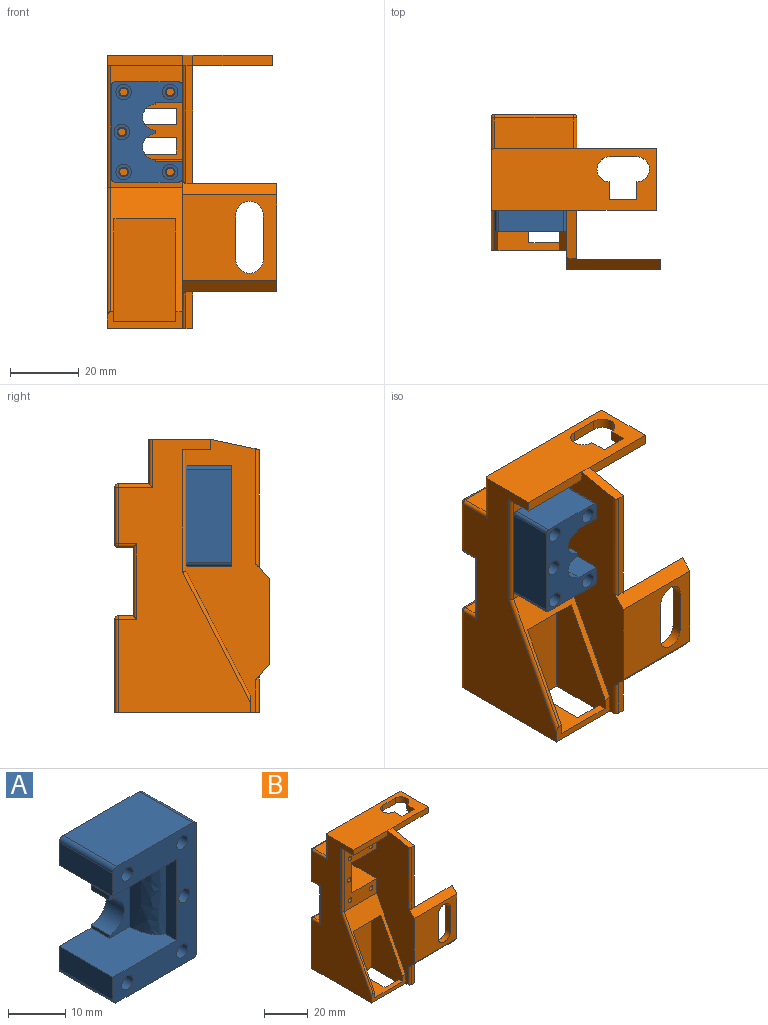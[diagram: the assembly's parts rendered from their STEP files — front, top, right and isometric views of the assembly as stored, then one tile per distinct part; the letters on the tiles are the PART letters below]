
ASSEMBLY  parts=2 mates=1
PART A: 36 faces, bbox 20.8x13.3x29.2 mm
  f0: extruded ~17.4x6mm, area 122.2mm2, adj f3,f5,f6,f14
  f1: plane 13.3x4.9mm, normal (-1,0,0), area 65.2mm2, adj f2,f3,f13,f34
  f2: plane 29.2x20.8mm, normal (0,-1,0), area 300.8mm2, adj f1,f3,f4,f5,f12,f14,f15,f16
  f3: plane 15.8x13.3mm, normal (0,0,-1), area 161.7mm2, adj f0,f1,f2,f6,f11,f13,f14
  f4: plane 13.3x4.9mm, normal (-1,0,0), area 65.2mm2, adj f2,f5,f13,f32
  f5: plane 15.8x13.3mm, normal (0,0,1), area 161.7mm2, adj f0,f2,f4,f6,f7,f13,f14
  f6: plane 17.4x5mm, normal (0,-1,0), area 42.8mm2, adj f0,f3,f5,f7,f8,f9,f10,f11
  f7: plane 4.5x0.65mm, normal (-1,0,0), area 2.9mm2, adj f5,f6,f8,f13
  f8: cylinder r=3.75mm len=7.5mm, axis (0,-1,0), area 53mm2, adj f6,f7,f9,f13
  f9: plane 4.5x1.1mm, normal (-1,0,0), area 5mm2, adj f6,f8,f10,f13
  f10: cylinder r=3.75mm len=7.5mm, axis (0,-1,0), area 53mm2, adj f6,f9,f11,f13
  f11: plane 4.5x0.65mm, normal (-1,0,0), area 2.9mm2, adj f3,f6,f10,f13
  f12: plane 27.2x13.3mm, normal (1,0,0), area 361.8mm2, adj f2,f13,f33,f35
  f13: plane 29.2x20.8mm, normal (0,1,0), area 345.3mm2, adj f1,f3,f4,f5,f7,f8,f9,f10
  f14: plane 17.4x2.8mm, normal (-1,0,0), area 48.7mm2, adj f0,f2,f3,f5
  f15: plane 18.8x13.3mm, normal (0,0,-1), area 250mm2, adj f2,f13,f32,f33
  f16: plane 18.8x13.3mm, normal (0,0,1), area 250mm2, adj f2,f13,f34,f35
  f17: cylinder r=2.25mm len=9.8mm, axis (0,1,0), area 138.5mm2, adj f13,f18
  f18: plane 4.5x4.5mm, normal (0,1,0), area 9.7mm2, adj f17,f31
  f19: cylinder r=2.25mm len=9.8mm, axis (0,1,0), area 138.5mm2, adj f13,f20
  f20: plane 4.5x4.5mm, normal (0,1,0), area 9.7mm2, adj f19,f30
  f21: cylinder r=2.25mm len=9.8mm, axis (0,1,0), area 138.5mm2, adj f13,f22
  f22: plane 4.5x4.5mm, normal (0,1,0), area 9.7mm2, adj f21,f29
  f23: cylinder r=2.25mm len=9.8mm, axis (0,1,0), area 138.5mm2, adj f13,f24
  f24: plane 4.5x4.5mm, normal (0,1,0), area 9.7mm2, adj f23,f28
  f25: cylinder r=2.25mm len=9.8mm, axis (0,1,0), area 138.5mm2, adj f13,f26
  f26: plane 4.5x4.5mm, normal (0,1,0), area 9.7mm2, adj f25,f27
  f27: cylinder r=1.4mm len=3.5mm, axis (0,1,0), area 30.8mm2, adj f2,f26
  f28: cylinder r=1.4mm len=3.5mm, axis (0,1,0), area 30.8mm2, adj f2,f24
  f29: cylinder r=1.4mm len=3.5mm, axis (0,1,0), area 30.8mm2, adj f2,f22
  f30: cylinder r=1.4mm len=3.5mm, axis (0,1,0), area 30.8mm2, adj f2,f20
  f31: cylinder r=1.4mm len=3.5mm, axis (0,1,0), area 30.8mm2, adj f2,f18
  f32: cylinder r=1mm len=13.3mm, axis (0,1,0), area 20.9mm2, adj f2,f4,f13,f15
  f33: cylinder r=1mm len=13.3mm, axis (0,1,0), area 20.9mm2, adj f2,f12,f13,f15
  f34: cylinder r=1mm len=13.3mm, axis (0,-1,0), area 20.9mm2, adj f1,f2,f13,f16
  f35: cylinder r=1mm len=13.3mm, axis (0,-1,0), area 20.9mm2, adj f2,f12,f13,f16
PART B: 94 faces, bbox 49.5x45.1x79.7 mm
  f0: plane 23.15x3mm, normal (0,-1,0), area 69.5mm2, adj f7,f40,f47,f50
  f1: plane 27.2x23mm, normal (0,1,0), area 625.6mm2, adj f30,f66,f68,f69
  f2: plane 79.7x38.6mm, normal (-1,0,0), area 1695.4mm2, adj f6,f30,f46,f50,f51,f68,f73,f77
  f3: plane 23x16.5mm, normal (0,1,0), area 261.4mm2, adj f16,f17,f18,f19,f20,f21,f22,f23
  f4: plane 10.7x2mm, normal (0,-1,0), area 21.4mm2, adj f7,f30,f39,f88
  f5: plane 34.4x2mm, normal (0,-1,0), area 68.8mm2, adj f7,f38,f89,f93
  f6: plane 22x5mm, normal (0,-1,0), area 55.5mm2, adj f2,f8,f12,f13,f27,f28,f30,f91
  f7: plane 79.7x41.1mm, normal (1,0,0), area 2953.5mm2, adj f0,f4,f5,f30,f31,f40,f48,f66
  f8: plane 32x20mm, normal (-1,0,0), area 446mm2, adj f6,f9,f11,f12,f28,f29,f30
  f9: plane 32x18mm, normal (0,-1,0), area 558mm2, adj f8,f10,f27,f28,f29,f30
  f10: plane 17.65x2mm, normal (1,0,0), area 35.3mm2, adj f9,f11,f28,f30
  f11: plane 9x2mm, normal (0,1,0), area 18mm2, adj f8,f10,f28,f30
  f12: plane 36.2x21mm, normal (0,-0.89,0.46), area 309mm2, adj f6,f8,f13,f14,f27,f29,f91
  f13: plane 79.7x42.3mm, normal (-1,0,0), area 1563.9mm2, adj f6,f12,f14,f15,f24,f26,f30,f37
  f14: plane 35.5x21mm, normal (0,-1,0), area 455.9mm2, adj f12,f13,f24,f25,f26,f51,f53,f55
  f15: plane 16.8x16mm, normal (0,-1,0), area 150.7mm2, adj f13,f16,f17,f18,f19,f20,f21,f22
  f16: plane 4.8x2.8mm, normal (-1,0,0), area 13.4mm2, adj f3,f15,f17,f22
  f17: plane 12.3x2.8mm, normal (0,0,1), area 34.4mm2, adj f3,f15,f16,f18
  f18: plane 4.8x2.8mm, normal (1,0,0), area 13.4mm2, adj f3,f15,f17,f22
  f19: plane 4.8x2.8mm, normal (-1,0,0), area 13.4mm2, adj f3,f15,f20,f23
  f20: plane 12.3x2.8mm, normal (0,0,1), area 34.4mm2, adj f3,f15,f19,f21
  f21: plane 4.8x2.8mm, normal (1,0,0), area 13.4mm2, adj f3,f15,f20,f23
  f22: plane 12.3x2.8mm, normal (0,0,-1), area 34.4mm2, adj f3,f15,f16,f18
  f23: plane 12.3x2.8mm, normal (0,0,-1), area 34.4mm2, adj f3,f15,f19,f21
  f24: plane 18x16mm, normal (0,0,1), area 288mm2, adj f13,f14,f15,f25
  f25: plane 18x16.8mm, normal (1,0,0), area 302.4mm2, adj f14,f15,f24,f26
  f26: plane 18x16mm, normal (0,0,-1), area 288mm2, adj f13,f14,f15,f25
  f27: plane 30x20mm, normal (1,0,0), area 410.7mm2, adj f6,f9,f12,f28,f29
  f28: plane 20x18mm, normal (0,0,1), area 201.2mm2, adj f6,f8,f9,f10,f11,f27
  f29: plane 18x5.98mm, normal (0,0,-1), area 107.6mm2, adj f8,f9,f12,f27
  f30: plane 42.1x25mm, normal (0,0,-1), area 838mm2, adj f1,f2,f4,f6,f7,f8,f9,f10
  f31: plane 31.6x24.5mm, normal (0,1,0), area 619.9mm2, adj f7,f32,f33,f34,f35,f36,f38,f39
  f32: cylinder r=4mm len=8mm, axis (0,1,0), area 37.7mm2, adj f31,f33,f36,f37
  f33: plane 13x3mm, normal (-1,0,0), area 39mm2, adj f31,f32,f34,f37
  f34: cylinder r=4mm len=8mm, axis (0,1,0), area 37.7mm2, adj f31,f33,f36,f37
  f35: plane 31.6x3mm, normal (1,0,0), area 84.9mm2, adj f31,f37,f38,f39
  f36: plane 13x3mm, normal (1,0,0), area 39mm2, adj f31,f32,f34,f37
  f37: plane 27.5x25mm, normal (0,-1,0), area 533.2mm2, adj f13,f32,f33,f34,f35,f36,f38,f39
  f38: plane 27.5x4.4mm, normal (0,-0.74,0.67), area 123mm2, adj f5,f13,f31,f35,f37,f89
  f39: plane 27.5x4.4mm, normal (0,-0.74,-0.67), area 123mm2, adj f4,f13,f31,f35,f37,f88
  f40: plane 23.15x18mm, normal (0,0,-1), area 276mm2, adj f0,f7,f41,f42,f43,f44,f45,f47
  f41: cylinder r=3.65mm len=7.3mm, axis (0,0,-1), area 34.4mm2, adj f40,f42,f49,f50
  f42: plane 8x3mm, normal (0,-1,0), area 24mm2, adj f40,f41,f43,f50
  f43: cylinder r=3.65mm len=7.3mm, axis (0,0,-1), area 34.4mm2, adj f40,f42,f44,f50
  f44: plane 5.05x3mm, normal (-1,0,0), area 15.2mm2, adj f40,f43,f45,f50
  f45: plane 8x3mm, normal (0,1,0), area 24mm2, adj f40,f44,f49,f50
  f46: plane 22x3mm, normal (0,-1,0), area 66mm2, adj f2,f13,f50,f51
  f47: plane 18x3mm, normal (1,0,0), area 54mm2, adj f0,f40,f48,f50
  f48: plane 47.15x14mm, normal (0,1,0), area 381.7mm2, adj f7,f40,f47,f50,f52,f76,f80
  f49: plane 5.05x3mm, normal (1,0,0), area 15.2mm2, adj f40,f41,f45,f50
  f50: plane 48.15x18mm, normal (0,0,1), area 725.8mm2, adj f0,f2,f41,f42,f43,f44,f45,f46
  f51: plane 22x8.2mm, normal (0,0,-1), area 158.6mm2, adj f2,f13,f14,f46,f90
  f52: plane 23x9mm, normal (0,0,1), area 207mm2, adj f48,f76,f83,f84
  f53: cylinder r=1.15mm len=5mm, axis (0,-1,0), area 36.1mm2, adj f14,f54
  f54: plane 2.3x2.3mm, normal (0,-1,0), area 4.2mm2, adj f53
  f55: cylinder r=1.15mm len=5mm, axis (0,-1,0), area 36.1mm2, adj f14,f56
  f56: plane 2.3x2.3mm, normal (0,-1,0), area 4.2mm2, adj f55
  f57: cylinder r=1.15mm len=5mm, axis (0,-1,0), area 36.1mm2, adj f14,f58
  f58: plane 2.3x2.3mm, normal (0,-1,0), area 4.2mm2, adj f57
  f59: cylinder r=1.15mm len=5mm, axis (0,-1,0), area 36.1mm2, adj f14,f60
  f60: plane 2.3x2.3mm, normal (0,-1,0), area 4.2mm2, adj f59
  f61: cylinder r=1.15mm len=5mm, axis (0,-1,0), area 36.1mm2, adj f14,f62
  f62: plane 2.3x2.3mm, normal (0,-1,0), area 4.2mm2, adj f61
  f63: plane 23x4.5mm, normal (0,0,-1), area 103.5mm2, adj f65,f74,f81,f82
  f64: plane 23x4.5mm, normal (0,0,1), area 103.5mm2, adj f65,f69,f70,f73
  f65: plane 23x20mm, normal (0,1,0), area 460mm2, adj f63,f64,f72,f77
  f66: cylinder r=1mm len=27.2mm, axis (0,0,1), area 42.7mm2, adj f1,f7,f30,f67
  f67: sphere r=1mm, area 1.6mm2, adj f66,f69,f70
  f68: cylinder r=1mm len=27.2mm, axis (0,0,-1), area 42.7mm2, adj f1,f2,f30,f71
  f69: cylinder r=1mm len=23mm, axis (-1,0,0), area 36.1mm2, adj f1,f64,f67,f71
  f70: cylinder r=1mm len=5.5mm, axis (0,1,0), area 7.6mm2, adj f7,f64,f67,f72
  f71: sphere r=1mm, area 1.6mm2, adj f68,f69,f73
  f72: cylinder r=1mm len=22mm, axis (0,0,-1), area 32.6mm2, adj f7,f65,f70,f74
  f73: cylinder r=1mm len=5.5mm, axis (0,-1,0), area 7.6mm2, adj f2,f64,f71,f77
  f74: cylinder r=1mm len=5.5mm, axis (0,-1,0), area 7.6mm2, adj f7,f63,f72,f78
  f75: cylinder r=1mm len=16.5mm, axis (0,0,1), area 25.9mm2, adj f3,f7,f78,f79
  f76: cylinder r=1mm len=9mm, axis (0,-1,0), area 14.1mm2, adj f7,f48,f52,f79
  f77: cylinder r=1mm len=22mm, axis (0,0,1), area 32.6mm2, adj f2,f65,f73,f81
  f78: sphere r=1mm, area 1.6mm2, adj f74,f75,f82
  f79: sphere r=1mm, area 1.6mm2, adj f75,f76,f83
  f80: cylinder r=1mm len=14mm, axis (0,0,-1), area 21mm2, adj f2,f48,f50,f84
  f81: cylinder r=1mm len=5.5mm, axis (0,1,0), area 7.6mm2, adj f2,f63,f77,f85
  f82: cylinder r=1mm len=23mm, axis (1,0,0), area 36.1mm2, adj f3,f63,f78,f85
  f83: cylinder r=1mm len=23mm, axis (1,0,0), area 36.1mm2, adj f3,f52,f79,f86
  f84: cylinder r=1mm len=10mm, axis (0,1,0), area 14.7mm2, adj f2,f52,f80,f86
  f85: sphere r=1mm, area 1.6mm2, adj f81,f82,f87
  f86: sphere r=1mm, area 1.6mm2, adj f83,f84,f87
  f87: cylinder r=1mm len=16.5mm, axis (0,0,-1), area 25.9mm2, adj f2,f3,f85,f86
  f88: cylinder r=1mm len=10.7mm, axis (0,0,-1), area 16.2mm2, adj f4,f13,f30,f39
  f89: cylinder r=1mm len=34.4mm, axis (0,0,-1), area 53.4mm2, adj f5,f13,f38,f92
  f90: cylinder r=1mm len=35.74mm, axis (0,0,1), area 55.9mm2, adj f2,f14,f51,f91
  f91: cylinder r=1mm len=38.59mm, axis (0,0.46,0.89), area 65.3mm2, adj f2,f6,f12,f90
  f92: plane 1x1mm, normal (0,0,-1), area 0.2mm2, adj f13,f89,f93
  f93: plane 14.1x3mm, normal (0,-0.21,0.98), area 43.2mm2, adj f5,f7,f13,f50,f92
PLACE A rot(axis=(0,0,1),180deg) t=(-7.07,6.21,29.29)mm
PLACE B t=(-8.67,23.31,-8.21)mm fixed
MATE fastened B.f55 <-> A.f17  axis (0,-1,0) through (-16.37,2.51,27.94)mm
